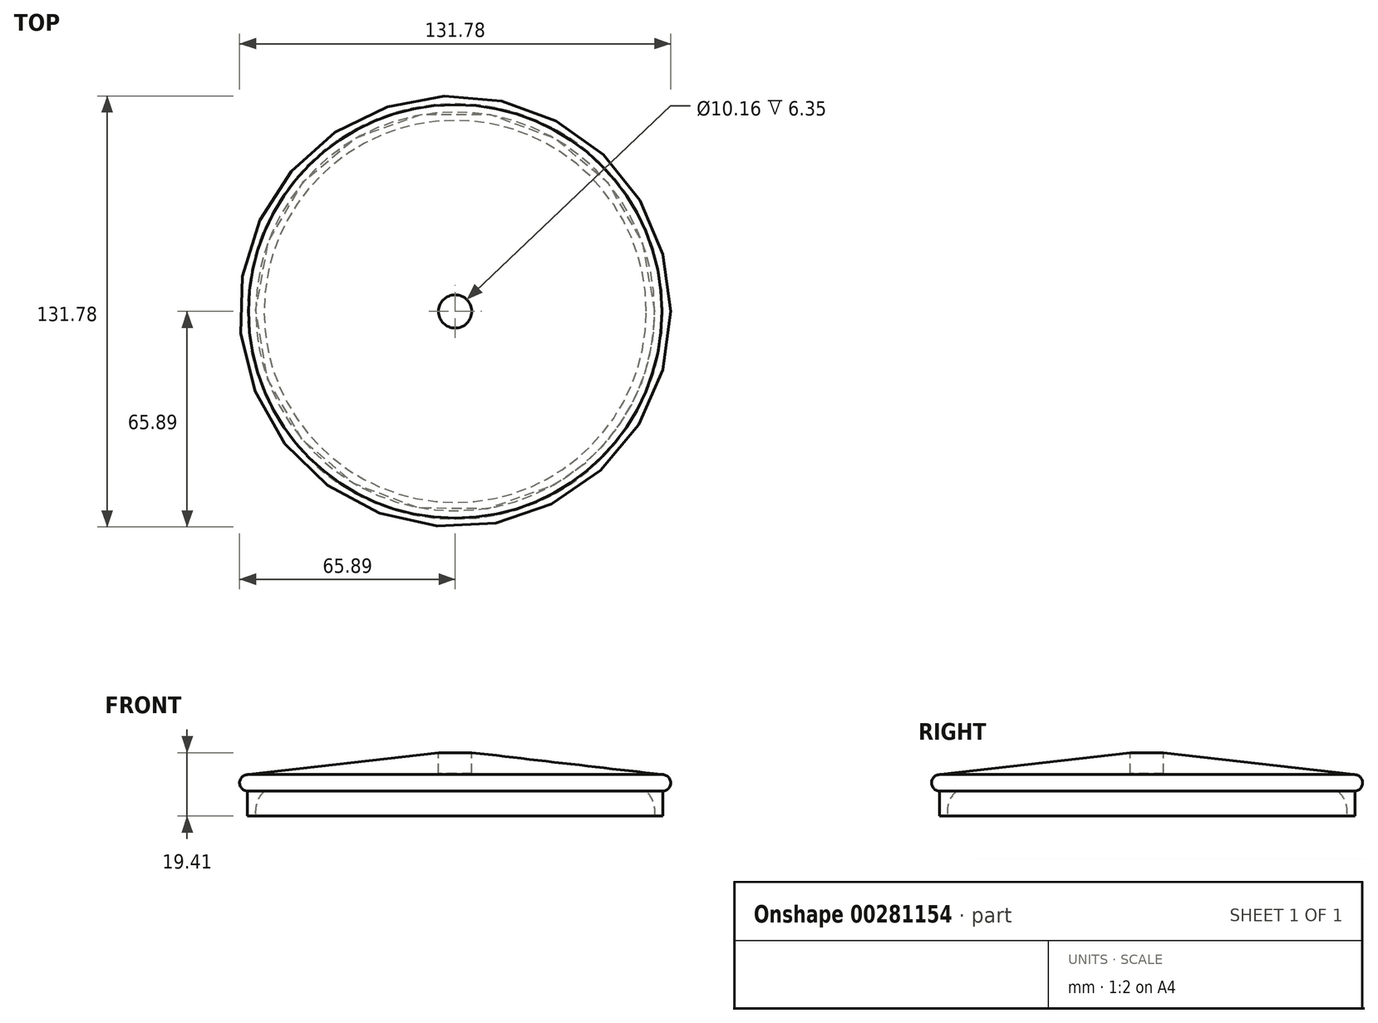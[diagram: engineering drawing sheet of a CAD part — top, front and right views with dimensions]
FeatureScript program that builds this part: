
annotation { "Feature Type Name" : "Feature", "Feature Type Description" : "" }
export const myFeature = defineFeature(function(context is Context, id is Id, definition is map)
    precondition{}
    {
        {
            var Q0;
            Q0=qCreatedBy(makeId("Front.planeOp"),FACE);
            var sketch = newSketch(context, id + "F0", { "sketchPlane" : qUnion([Q0])});
            skLineSegment(sketch, "E0", {"start": v(0, 7.62) * mm, "end": v(58.41, 7.62) * mm});
            skLineSegment(sketch, "E1", {"start": v(0, 13.06) * mm, "end": v(0, 7.62) * mm});
            skArc(sketch, "E2", {"start": v(63.5, 7.62) * mm, "mid": v(65.89, 10.31) * mm, "end": v(63.2, 12.7) * mm});
            skLineSegment(sketch, "E3", {"start": v(63.5, 7.62) * mm, "end": v(63.5, 0) * mm});
            skLineSegment(sketch, "E4", {"start": v(0, 13.06) * mm, "end": v(5.08, 13.06) * mm});
            skLineSegment(sketch, "E5", {"start": v(5.08, 13.06) * mm, "end": v(5.08, 19.4) * mm});
            skLineSegment(sketch, "E6", {"start": v(5.08, 19.4) * mm, "end": v(63.2, 12.7) * mm});
            skArc(sketch, "E7", {"start": v(60.96, 0) * mm, "mid": v(60.6, 4.12) * mm, "end": v(58.41, 7.62) * mm});
            skLineSegment(sketch, "E8", {"start": v(60.96, 0) * mm, "end": v(63.5, 0) * mm});
            skSolve(sketch);
        }
        {
            var Q0;
            Q0 = qSketchRegion(id + "F0", true);
            var Q1;
            Q1=sQuery(id+"F0.wireOp",EDGE,"E1");
            revolve(context, id + "F1", {"entities" : qUnion([Q0]), "axis" : qUnion([Q1]), "revolveType" : RevolveType.FULL});
        }
    });
